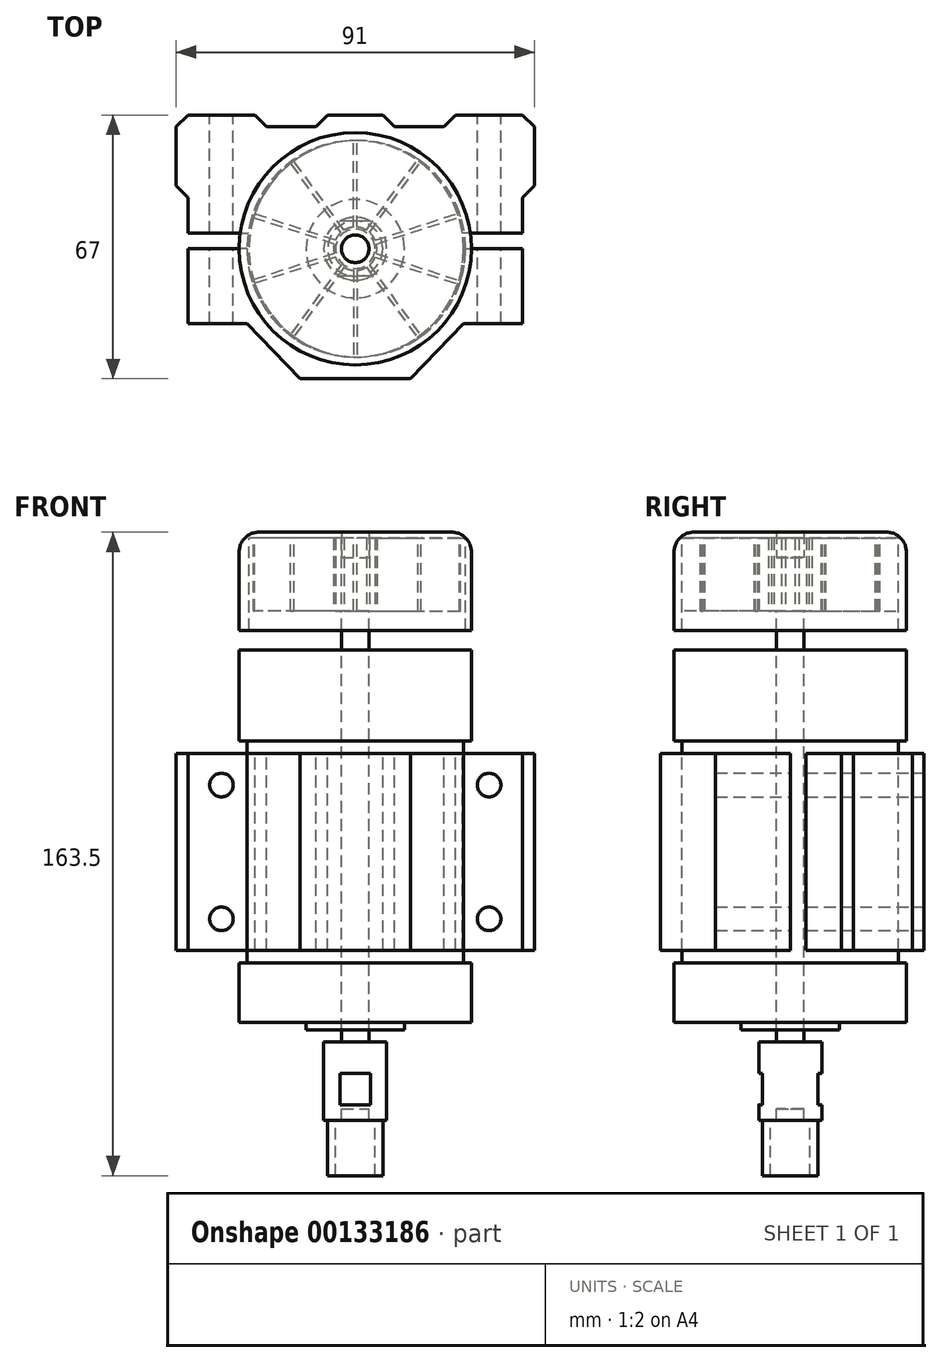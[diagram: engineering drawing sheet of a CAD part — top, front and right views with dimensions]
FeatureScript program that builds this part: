
annotation { "Feature Type Name" : "Feature", "Feature Type Description" : "" }
export const myFeature = defineFeature(function(context is Context, id is Id, definition is map)
    precondition{}
    {
        {
            var Q0;
            Q0=qCreatedBy(makeId("Top.planeOp"),FACE);
            var sketch = newSketch(context, id + "F0", { "sketchPlane" : qUnion([Q0])});
            skCircle(sketch, "E0", {"center": v(0, 0) * mm, "radius": 27.5 * mm});
            skLineSegment(sketch, "E1", {"start": v(-27.5, 0) * mm, "end": v(-42.5, 0) * mm});
            skLineSegment(sketch, "E2", {"start": v(-42.5, 0) * mm, "end": v(-42.5, -19) * mm});
            skLineSegment(sketch, "E3", {"start": v(-42.5, -19) * mm, "end": v(-27.5, -19) * mm});
            skLineSegment(sketch, "E4", {"start": v(-27.5, -19) * mm, "end": v(-14, -33) * mm});
            skLineSegment(sketch, "E5", {"start": v(-14, -33) * mm, "end": v(0, -33) * mm});
            skLineSegment(sketch, "E6.MirrorCS", {"start": v(14, -33) * mm, "end": v(0, -33) * mm});
            skLineSegment(sketch, "E7.MirrorCS", {"start": v(27.5, -19) * mm, "end": v(14, -33) * mm});
            skLineSegment(sketch, "E8.MirrorCS", {"start": v(42.5, -19) * mm, "end": v(27.5, -19) * mm});
            skLineSegment(sketch, "E9.MirrorCS", {"start": v(27.5, 0) * mm, "end": v(42.5, 0) * mm});
            skLineSegment(sketch, "E10.MirrorCS", {"start": v(42.5, 0) * mm, "end": v(42.5, -19) * mm});
            skLineSegment(sketch, "E11", {"start": v(-42.5, 4) * mm, "end": v(-42.5, 13) * mm});
            skLineSegment(sketch, "E12", {"start": v(-42.5, 13) * mm, "end": v(-45.5, 16) * mm});
            skLineSegment(sketch, "E13", {"start": v(-45.5, 16) * mm, "end": v(-45.5, 31) * mm});
            skLineSegment(sketch, "E14", {"start": v(-45.5, 31) * mm, "end": v(-42.5, 34) * mm});
            skLineSegment(sketch, "E15", {"start": v(-42.5, 34) * mm, "end": v(-25.5, 34) * mm});
            skLineSegment(sketch, "E16", {"start": v(-25.5, 34) * mm, "end": v(-22.5, 31) * mm});
            skLineSegment(sketch, "E17", {"start": v(-22.5, 31) * mm, "end": v(-10, 31) * mm});
            skLineSegment(sketch, "E18", {"start": v(-10, 31) * mm, "end": v(-7, 34) * mm});
            skLineSegment(sketch, "E19", {"start": v(-7, 34) * mm, "end": v(0, 34) * mm});
            skLineSegment(sketch, "E20", {"start": v(-42.5, 4) * mm, "end": v(-27.2, 4) * mm});
            skLineSegment(sketch, "E21.MirrorCS", {"start": v(25.5, 34) * mm, "end": v(22.5, 31) * mm});
            skLineSegment(sketch, "E22.MirrorCS", {"start": v(42.5, 34) * mm, "end": v(25.5, 34) * mm});
            skLineSegment(sketch, "E23.MirrorCS", {"start": v(45.5, 31) * mm, "end": v(42.5, 34) * mm});
            skLineSegment(sketch, "E24.MirrorCS", {"start": v(45.5, 16) * mm, "end": v(45.5, 31) * mm});
            skLineSegment(sketch, "E25.MirrorCS", {"start": v(7, 34) * mm, "end": v(0, 34) * mm});
            skLineSegment(sketch, "E26.MirrorCS", {"start": v(10, 31) * mm, "end": v(7, 34) * mm});
            skLineSegment(sketch, "E27.MirrorCS", {"start": v(22.5, 31) * mm, "end": v(10, 31) * mm});
            skLineSegment(sketch, "E28.MirrorCS", {"start": v(42.5, 13) * mm, "end": v(45.5, 16) * mm});
            skLineSegment(sketch, "E29.MirrorCS", {"start": v(42.5, 4) * mm, "end": v(42.5, 13) * mm});
            skLineSegment(sketch, "E30.MirrorCS", {"start": v(42.5, 4) * mm, "end": v(27.2, 4) * mm});
            skSolve(sketch);
        }
        {
            var Q0;
            Q0=makeQuery(id+"F0.imprint","IMPRINT",FACE,{"disambiguationData":[TD([[makeQuery(id+"F0.imprint","IMPRINT",EDGE,{"derivedFrom":sQuery(id+"F0.wireOp",EDGE,"E0")}),1.0]])]});
            extrude(context, id + "F1", {"entities" : qUnion([Q0]), "oppositeDirection" : true, "depth" : 56.5 * mm, "symmetric" : true});
        }
        {
            var Q0;
            Q0=makeQuery(id+"F1.opExtrude","CAP_FACE",FACE,{"disambiguationData":[OSD([sQuery(id+"F0.wireOp",EDGE,"E0")])],"isStart":true});
            var sketch = newSketch(context, id + "F2", { "sketchPlane" : qUnion([Q0])});
            skCircle(sketch, "E31.0", {"center": v(0, 0) * mm, "radius": 29.5 * mm});
            skSolve(sketch);
        }
        {
            var Q0;
            Q0=makeQuery(id+"F2.imprint","IMPRINT",FACE,{"disambiguationData":[TD([[makeQuery(id+"F2.imprint","IMPRINT",EDGE,{"derivedFrom":sQuery(id+"F2.wireOp",EDGE,"E31.0")}),1.0]])]});
            var Q1;
            Q1=makeQuery(id+"F2.imprint","IMPRINT",FACE,{"disambiguationData":[TD([[makeQuery(id+"F2.imprint","IMPRINT",EDGE,{"derivedFrom":makeQuery(id+"F1.opExtrude","CAP_EDGE",EDGE,{"disambiguationData":[OSD([sQuery(id+"F0.wireOp",EDGE,"E0")])],"isStart":true})}),1.0]])]});
            extrude(context, id + "F3", {"entities" : qUnion([Q0, Q1]), "operationType" : NewBodyOperationType.ADD, "depth" : 23 * mm});
        }
        {
            var Q0;
            Q0=makeQuery(id+"F1.opExtrude","CAP_FACE",FACE,{"disambiguationData":[OSD([sQuery(id+"F0.wireOp",EDGE,"E0")])],"isStart":false});
            var sketch = newSketch(context, id + "F4", { "sketchPlane" : qUnion([Q0])});
            skCircle(sketch, "E32.0", {"center": v(0, 0) * mm, "radius": 29.5 * mm});
            skSolve(sketch);
        }
        {
            var Q0;
            Q0=makeQuery(id+"F4.imprint","IMPRINT",FACE,{"disambiguationData":[TD([[makeQuery(id+"F4.imprint","IMPRINT",EDGE,{"derivedFrom":sQuery(id+"F4.wireOp",EDGE,"E32.0")}),1.0]])]});
            var Q1;
            Q1=makeQuery(id+"F4.imprint","IMPRINT",FACE,{"disambiguationData":[TD([[makeQuery(id+"F4.imprint","IMPRINT",EDGE,{"derivedFrom":makeQuery(id+"F1.opExtrude","CAP_EDGE",EDGE,{"disambiguationData":[OSD([sQuery(id+"F0.wireOp",EDGE,"E0")])],"isStart":false})}),-1.0]])]});
            extrude(context, id + "F5", {"entities" : qUnion([Q0, Q1]), "operationType" : NewBodyOperationType.ADD, "depth" : 15 * mm});
        }
        {
            var Q0;
            Q0=makeQuery(id+"F5.opExtrude","CAP_FACE",FACE,{"disambiguationData":[OSD([sQuery(id+"F4.wireOp",EDGE,"E32.0")])],"isStart":false});
            var sketch = newSketch(context, id + "F6", { "sketchPlane" : qUnion([Q0])});
            skCircle(sketch, "E33", {"center": v(0, 0) * mm, "radius": 12.5 * mm});
            skSolve(sketch);
        }
        {
            var Q0;
            Q0=makeQuery(id+"F6.imprint","IMPRINT",FACE,{"disambiguationData":[TD([[makeQuery(id+"F6.imprint","IMPRINT",EDGE,{"derivedFrom":sQuery(id+"F6.wireOp",EDGE,"E33")}),1.0]])]});
            extrude(context, id + "F7", {"entities" : qUnion([Q0]), "operationType" : NewBodyOperationType.ADD, "depth" : 2 * mm});
        }
        {
            var Q0;
            Q0=makeQuery(id+"F7.opExtrude","CAP_FACE",FACE,{"disambiguationData":[OSD([sQuery(id+"F6.wireOp",EDGE,"E33")])],"isStart":false});
            var sketch = newSketch(context, id + "F8", { "sketchPlane" : qUnion([Q0])});
            skCircle(sketch, "E34", {"center": v(0, 0) * mm, "radius": 3.5 * mm});
            skSolve(sketch);
        }
        {
            var Q0;
            Q0=makeQuery(id+"F8.imprint","IMPRINT",FACE,{"disambiguationData":[TD([[makeQuery(id+"F8.imprint","IMPRINT",EDGE,{"derivedFrom":sQuery(id+"F8.wireOp",EDGE,"E34")}),1.0]])]});
            extrude(context, id + "F9", {"entities" : qUnion([Q0]), "depth" : 20 * mm, "hasSecondDirection" : true, "secondDirectionOppositeDirection" : true, "secondDirectionDepth" : 120 * mm});
        }
        {
            var Q0;
            Q0=makeQuery(id+"F7.opExtrude","CAP_FACE",FACE,{"disambiguationData":[OSD([sQuery(id+"F6.wireOp",EDGE,"E33")])],"isStart":false});
            cPlane(context, id + "F10", {"entities" : qUnion([Q0]), "cplaneType" : CPlaneType.OFFSET, "offset" : 3 * mm, "width" : 150 * mm, "height" : 150 * mm});
        }
        {
            var Q0;
            Q0=qCreatedBy(id+"F10.planeOp",FACE);
            var sketch = newSketch(context, id + "F11", { "sketchPlane" : qUnion([Q0])});
            skCircle(sketch, "E35", {"center": v(0, 0) * mm, "radius": 8 * mm});
            skCircle(sketch, "E36", {"center": v(0, 0) * mm, "radius": 3.5 * mm});
            skSolve(sketch);
        }
        {
            var Q0;
            Q0=makeQuery(id+"F11.imprint","IMPRINT",FACE,{"disambiguationData":[TD([[makeQuery(id+"F11.imprint","IMPRINT",EDGE,{"derivedFrom":sQuery(id+"F11.wireOp",EDGE,"E35")}),1.0]])]});
            extrude(context, id + "F12", {"entities" : qUnion([Q0]), "operationType" : NewBodyOperationType.ADD, "depth" : 20 * mm});
        }
        {
            var Q0;
            Q0=qCreatedBy(makeId("Right.planeOp"),FACE);
            var sketch = newSketch(context, id + "F13", { "sketchPlane" : qUnion([Q0])});
            skLineSegment(sketch, "E37.bottom", {"start": v(12.32, -56.25) * mm, "end": v(7, -56.25) * mm});
            skLineSegment(sketch, "E37.top", {"start": v(12.32, -64.25) * mm, "end": v(7, -64.25) * mm});
            skLineSegment(sketch, "E37.left", {"start": v(12.32, -56.25) * mm, "end": v(12.32, -64.25) * mm});
            skLineSegment(sketch, "E37.right", {"start": v(7, -56.25) * mm, "end": v(7, -64.25) * mm});
            skLineSegment(sketch, "E38", {"start": v(0, -59.62) * mm, "end": v(0, -108.48) * mm, "construction": true});
            skLineSegment(sketch, "E39.MirrorCS", {"start": v(-12.32, -56.25) * mm, "end": v(-7, -56.25) * mm});
            skLineSegment(sketch, "E40.MirrorCS", {"start": v(-12.32, -64.25) * mm, "end": v(-7, -64.25) * mm});
            skLineSegment(sketch, "E41.MirrorCS", {"start": v(-12.32, -56.25) * mm, "end": v(-12.32, -64.25) * mm});
            skLineSegment(sketch, "E42.MirrorCS", {"start": v(-7, -56.25) * mm, "end": v(-7, -64.25) * mm});
            skSolve(sketch);
        }
        {
            var Q0;
            Q0=makeQuery(id+"F13.imprint","IMPRINT",FACE,{"disambiguationData":[TD([[makeQuery(id+"F13.imprint","IMPRINT",EDGE,{"derivedFrom":sQuery(id+"F13.wireOp",EDGE,"E37.bottom")}),1.0]])]});
            var Q1;
            Q1=makeQuery(id+"F13.imprint","IMPRINT",FACE,{"disambiguationData":[TD([[makeQuery(id+"F13.imprint","IMPRINT",EDGE,{"derivedFrom":sQuery(id+"F13.wireOp",EDGE,"E39.MirrorCS")}),-1.0]])]});
            extrude(context, id + "F14", {"entities" : qUnion([Q0, Q1]), "operationType" : NewBodyOperationType.REMOVE, "depth" : 10 * mm, "symmetric" : true});
        }
        {
            var Q0;
            Q0=makeQuery(id+"F12.opExtrude","CAP_FACE",FACE,{"disambiguationData":[OSD([sQuery(id+"F11.wireOp",EDGE,"E35"),sQuery(id+"F11.wireOp",EDGE,"E36")])],"isStart":false});
            var sketch = newSketch(context, id + "F15", { "sketchPlane" : qUnion([Q0])});
            skCircle(sketch, "E43", {"center": v(0, 0) * mm, "radius": 7 * mm});
            skCircle(sketch, "E44.0", {"center": v(0, 0) * mm, "radius": 5 * mm});
            skSolve(sketch);
        }
        {
            var Q0;
            Q0=makeQuery(id+"F15.imprint","IMPRINT",FACE,{"disambiguationData":[TD([[makeQuery(id+"F15.imprint","IMPRINT",EDGE,{"derivedFrom":sQuery(id+"F15.wireOp",EDGE,"E43")}),1.0]])]});
            extrude(context, id + "F16", {"entities" : qUnion([Q0]), "operationType" : NewBodyOperationType.ADD, "depth" : 14 * mm});
        }
        {
            var Q0;
            Q0=makeQuery(id+"F3.opExtrude","CAP_FACE",FACE,{"disambiguationData":[OSD([sQuery(id+"F2.wireOp",EDGE,"E31.0")])],"isStart":false});
            cPlane(context, id + "F17", {"entities" : qUnion([Q0]), "cplaneType" : CPlaneType.OFFSET, "offset" : 10 * mm, "width" : 150 * mm, "height" : 150 * mm});
        }
        {
            var Q0;
            Q0=qCreatedBy(id+"F17.planeOp",FACE);
            var sketch = newSketch(context, id + "F18", { "sketchPlane" : qUnion([Q0])});
            skLineSegment(sketch, "E45.bottom", {"start": v(-0.5, -3.78) * mm, "end": v(0.5, -3.78) * mm});
            skLineSegment(sketch, "E45.top", {"start": v(-0.5, -29.13) * mm, "end": v(0.5, -29.13) * mm});
            skLineSegment(sketch, "E45.left", {"start": v(-0.5, -5.48) * mm, "end": v(-0.5, -29.13) * mm});
            skLineSegment(sketch, "E45.right", {"start": v(0.5, -5.48) * mm, "end": v(0.5, -29.13) * mm});
            skLineSegment(sketch, "E46.1.0", {"start": v(3.62, -4.14) * mm, "end": v(17.53, -23.27) * mm});
            skLineSegment(sketch, "E46.1.1", {"start": v(2.81, -4.73) * mm, "end": v(16.72, -23.86) * mm});
            skLineSegment(sketch, "E46.1.2", {"start": v(16.72, -23.86) * mm, "end": v(17.53, -23.27) * mm});
            skLineSegment(sketch, "E46.1.3", {"start": v(1.82, -3.35) * mm, "end": v(2.63, -2.76) * mm});
            skLineSegment(sketch, "E46.2.0", {"start": v(5.36, -1.22) * mm, "end": v(27.86, -8.53) * mm});
            skLineSegment(sketch, "E46.2.1", {"start": v(5.05, -2.17) * mm, "end": v(27.55, -9.48) * mm});
            skLineSegment(sketch, "E46.2.2", {"start": v(27.55, -9.48) * mm, "end": v(27.86, -8.53) * mm});
            skLineSegment(sketch, "E46.2.3", {"start": v(3.44, -1.64) * mm, "end": v(3.75, -0.7) * mm});
            skLineSegment(sketch, "E46.3.0", {"start": v(5.05, 2.17) * mm, "end": v(27.55, 9.48) * mm});
            skLineSegment(sketch, "E46.3.1", {"start": v(5.36, 1.22) * mm, "end": v(27.86, 8.53) * mm});
            skLineSegment(sketch, "E46.3.2", {"start": v(27.86, 8.53) * mm, "end": v(27.55, 9.48) * mm});
            skLineSegment(sketch, "E46.3.3", {"start": v(3.75, 0.7) * mm, "end": v(3.44, 1.64) * mm});
            skLineSegment(sketch, "E46.4.0", {"start": v(2.81, 4.73) * mm, "end": v(16.72, 23.86) * mm});
            skLineSegment(sketch, "E46.4.1", {"start": v(3.62, 4.14) * mm, "end": v(17.53, 23.27) * mm});
            skLineSegment(sketch, "E46.4.2", {"start": v(17.53, 23.27) * mm, "end": v(16.72, 23.86) * mm});
            skLineSegment(sketch, "E46.4.3", {"start": v(2.63, 2.76) * mm, "end": v(1.82, 3.35) * mm});
            skLineSegment(sketch, "E46.5.0", {"start": v(-0.5, 5.48) * mm, "end": v(-0.5, 29.13) * mm});
            skLineSegment(sketch, "E46.5.1", {"start": v(0.5, 5.48) * mm, "end": v(0.5, 29.13) * mm});
            skLineSegment(sketch, "E46.5.2", {"start": v(0.5, 29.13) * mm, "end": v(-0.5, 29.13) * mm});
            skLineSegment(sketch, "E46.5.3", {"start": v(0.5, 3.78) * mm, "end": v(-0.5, 3.78) * mm});
            skLineSegment(sketch, "E46.6.0", {"start": v(-3.62, 4.14) * mm, "end": v(-17.53, 23.27) * mm});
            skLineSegment(sketch, "E46.6.1", {"start": v(-2.81, 4.73) * mm, "end": v(-16.72, 23.86) * mm});
            skLineSegment(sketch, "E46.6.2", {"start": v(-16.72, 23.86) * mm, "end": v(-17.53, 23.27) * mm});
            skLineSegment(sketch, "E46.6.3", {"start": v(-1.82, 3.35) * mm, "end": v(-2.63, 2.76) * mm});
            skLineSegment(sketch, "E46.7.0", {"start": v(-5.36, 1.22) * mm, "end": v(-27.86, 8.53) * mm});
            skLineSegment(sketch, "E46.7.1", {"start": v(-5.05, 2.17) * mm, "end": v(-27.55, 9.48) * mm});
            skLineSegment(sketch, "E46.7.2", {"start": v(-27.55, 9.48) * mm, "end": v(-27.86, 8.53) * mm});
            skLineSegment(sketch, "E46.7.3", {"start": v(-3.44, 1.64) * mm, "end": v(-3.75, 0.7) * mm});
            skLineSegment(sketch, "E46.8.0", {"start": v(-5.05, -2.17) * mm, "end": v(-27.55, -9.48) * mm});
            skLineSegment(sketch, "E46.8.1", {"start": v(-5.36, -1.22) * mm, "end": v(-27.86, -8.53) * mm});
            skLineSegment(sketch, "E46.8.2", {"start": v(-27.86, -8.53) * mm, "end": v(-27.55, -9.48) * mm});
            skLineSegment(sketch, "E46.8.3", {"start": v(-3.75, -0.7) * mm, "end": v(-3.44, -1.64) * mm});
            skLineSegment(sketch, "E46.9.0", {"start": v(-2.81, -4.73) * mm, "end": v(-16.72, -23.86) * mm});
            skLineSegment(sketch, "E46.9.1", {"start": v(-3.62, -4.14) * mm, "end": v(-17.53, -23.27) * mm});
            skLineSegment(sketch, "E46.9.2", {"start": v(-17.53, -23.27) * mm, "end": v(-16.72, -23.86) * mm});
            skLineSegment(sketch, "E46.9.3", {"start": v(-2.63, -2.76) * mm, "end": v(-1.82, -3.35) * mm});
            skPoint(sketch, "E46.center", {"position": v(0, 0) * mm});
            skCircle(sketch, "E47", {"center": v(0, 0) * mm, "radius": 3.5 * mm});
            skArc(sketch, "E48", {"start": v(-5.36, 1.22) * mm, "mid": v(-5.5, 0) * mm, "end": v(-5.36, -1.22) * mm});
            skArc(sketch, "E49.trimOffspring", {"start": v(-3.62, 4.14) * mm, "mid": v(-4.45, 3.23) * mm, "end": v(-5.05, 2.17) * mm});
            skArc(sketch, "E50.trimOffspring", {"start": v(-0.5, 5.48) * mm, "mid": v(-1.7, 5.23) * mm, "end": v(-2.81, 4.73) * mm});
            skArc(sketch, "E51.trimOffspring", {"start": v(2.81, 4.73) * mm, "mid": v(1.7, 5.23) * mm, "end": v(0.5, 5.48) * mm});
            skArc(sketch, "E52.trimOffspring", {"start": v(5.05, 2.17) * mm, "mid": v(4.45, 3.23) * mm, "end": v(3.62, 4.14) * mm});
            skArc(sketch, "E53.trimOffspring", {"start": v(5.36, -1.22) * mm, "mid": v(5.5, 0) * mm, "end": v(5.36, 1.22) * mm});
            skArc(sketch, "E54.trimOffspring", {"start": v(3.62, -4.14) * mm, "mid": v(4.45, -3.23) * mm, "end": v(5.05, -2.17) * mm});
            skArc(sketch, "E55.trimOffspring", {"start": v(0.5, -5.48) * mm, "mid": v(1.7, -5.23) * mm, "end": v(2.81, -4.73) * mm});
            skArc(sketch, "E56.trimOffspring", {"start": v(-2.81, -4.73) * mm, "mid": v(-1.7, -5.23) * mm, "end": v(-0.5, -5.48) * mm});
            skArc(sketch, "E57.trimOffspring", {"start": v(-5.05, -2.17) * mm, "mid": v(-4.45, -3.23) * mm, "end": v(-3.62, -4.14) * mm});
            skSolve(sketch);
        }
        {
            var Q0;
            Q0=makeQuery(id+"F18.imprint","IMPRINT",FACE,{"disambiguationData":[TD([[makeQuery(id+"F18.imprint","IMPRINT",EDGE,{"derivedFrom":sQuery(id+"F18.wireOp",EDGE,"E45.top")}),1.0]])]});
            extrude(context, id + "F19", {"entities" : qUnion([Q0]), "operationType" : NewBodyOperationType.ADD, "depth" : 20 * mm});
        }
        {
            var Q0;
            Q0=makeQuery(id+"F19.opExtrude","CAP_FACE",FACE,{"disambiguationData":[OSD([sQuery(id+"F18.wireOp",EDGE,"E45.top"),sQuery(id+"F18.wireOp",EDGE,"E45.left"),sQuery(id+"F18.wireOp",EDGE,"E45.right"),sQuery(id+"F18.wireOp",EDGE,"E46.1.0"),sQuery(id+"F18.wireOp",EDGE,"E46.1.1"),sQuery(id+"F18.wireOp",EDGE,"E46.1.2"),sQuery(id+"F18.wireOp",EDGE,"E46.2.0"),sQuery(id+"F18.wireOp",EDGE,"E46.2.1"),sQuery(id+"F18.wireOp",EDGE,"E46.2.2"),sQuery(id+"F18.wireOp",EDGE,"E46.3.0"),sQuery(id+"F18.wireOp",EDGE,"E46.3.1"),sQuery(id+"F18.wireOp",EDGE,"E46.3.2"),sQuery(id+"F18.wireOp",EDGE,"E46.4.0"),sQuery(id+"F18.wireOp",EDGE,"E46.4.1"),sQuery(id+"F18.wireOp",EDGE,"E46.4.2"),sQuery(id+"F18.wireOp",EDGE,"E46.5.0"),sQuery(id+"F18.wireOp",EDGE,"E46.5.1"),sQuery(id+"F18.wireOp",EDGE,"E46.5.2"),sQuery(id+"F18.wireOp",EDGE,"E46.6.0"),sQuery(id+"F18.wireOp",EDGE,"E46.6.1"),sQuery(id+"F18.wireOp",EDGE,"E46.6.2"),sQuery(id+"F18.wireOp",EDGE,"E46.7.0"),sQuery(id+"F18.wireOp",EDGE,"E46.7.1"),sQuery(id+"F18.wireOp",EDGE,"E46.7.2"),sQuery(id+"F18.wireOp",EDGE,"E46.8.0"),sQuery(id+"F18.wireOp",EDGE,"E46.8.1"),sQuery(id+"F18.wireOp",EDGE,"E46.8.2"),sQuery(id+"F18.wireOp",EDGE,"E46.9.0"),sQuery(id+"F18.wireOp",EDGE,"E46.9.1"),sQuery(id+"F18.wireOp",EDGE,"E46.9.2"),sQuery(id+"F18.wireOp",EDGE,"E47"),sQuery(id+"F18.wireOp",EDGE,"E48"),sQuery(id+"F18.wireOp",EDGE,"E49.trimOffspring"),sQuery(id+"F18.wireOp",EDGE,"E50.trimOffspring"),sQuery(id+"F18.wireOp",EDGE,"E51.trimOffspring"),sQuery(id+"F18.wireOp",EDGE,"E52.trimOffspring"),sQuery(id+"F18.wireOp",EDGE,"E53.trimOffspring"),sQuery(id+"F18.wireOp",EDGE,"E54.trimOffspring"),sQuery(id+"F18.wireOp",EDGE,"E55.trimOffspring"),sQuery(id+"F18.wireOp",EDGE,"E56.trimOffspring"),sQuery(id+"F18.wireOp",EDGE,"E57.trimOffspring")])],"isStart":false});
            var sketch = newSketch(context, id + "F20", { "sketchPlane" : qUnion([Q0])});
            skCircle(sketch, "E58", {"center": v(0, 0) * mm, "radius": 29.5 * mm});
            skSolve(sketch);
        }
        {
            var Q0;
            Q0=makeQuery(id+"F20.imprint","IMPRINT",FACE,{"disambiguationData":[TD([[makeQuery(id+"F20.imprint","IMPRINT",EDGE,{"derivedFrom":sQuery(id+"F20.wireOp",EDGE,"E58")}),1.0]])]});
            extrude(context, id + "F21", {"entities" : qUnion([Q0]), "operationType" : NewBodyOperationType.ADD, "oppositeDirection" : true, "depth" : 1.5 * mm});
        }
        {
            var Q0;
            {var subQ0=sQuery(id+"F18.wireOp",EDGE,"E57.trimOffspring");var subQ1=sQuery(id+"F18.wireOp",EDGE,"E56.trimOffspring");var subQ2=sQuery(id+"F18.wireOp",EDGE,"E55.trimOffspring");var subQ3=sQuery(id+"F18.wireOp",EDGE,"E54.trimOffspring");var subQ4=sQuery(id+"F18.wireOp",EDGE,"E53.trimOffspring");var subQ5=sQuery(id+"F18.wireOp",EDGE,"E52.trimOffspring");var subQ6=sQuery(id+"F18.wireOp",EDGE,"E51.trimOffspring");var subQ7=sQuery(id+"F18.wireOp",EDGE,"E50.trimOffspring");var subQ8=sQuery(id+"F18.wireOp",EDGE,"E49.trimOffspring");var subQ9=sQuery(id+"F18.wireOp",EDGE,"E48");var subQ10=sQuery(id+"F18.wireOp",EDGE,"E46.9.2");var subQ11=sQuery(id+"F18.wireOp",EDGE,"E46.9.1");var subQ12=sQuery(id+"F18.wireOp",EDGE,"E46.9.0");var subQ13=sQuery(id+"F18.wireOp",EDGE,"E46.8.2");var subQ14=sQuery(id+"F18.wireOp",EDGE,"E46.8.1");var subQ15=sQuery(id+"F18.wireOp",EDGE,"E46.8.0");var subQ16=sQuery(id+"F18.wireOp",EDGE,"E46.7.2");var subQ17=sQuery(id+"F18.wireOp",EDGE,"E46.7.1");var subQ18=sQuery(id+"F18.wireOp",EDGE,"E46.7.0");var subQ19=sQuery(id+"F18.wireOp",EDGE,"E46.6.2");var subQ20=sQuery(id+"F18.wireOp",EDGE,"E46.6.1");var subQ21=sQuery(id+"F18.wireOp",EDGE,"E46.6.0");var subQ22=sQuery(id+"F18.wireOp",EDGE,"E46.5.2");var subQ23=sQuery(id+"F18.wireOp",EDGE,"E46.5.1");var subQ24=sQuery(id+"F18.wireOp",EDGE,"E46.5.0");var subQ25=sQuery(id+"F18.wireOp",EDGE,"E46.4.2");var subQ26=sQuery(id+"F18.wireOp",EDGE,"E46.4.1");var subQ27=sQuery(id+"F18.wireOp",EDGE,"E46.4.0");var subQ28=sQuery(id+"F18.wireOp",EDGE,"E46.3.2");var subQ29=sQuery(id+"F18.wireOp",EDGE,"E46.3.1");var subQ30=sQuery(id+"F18.wireOp",EDGE,"E46.3.0");var subQ31=sQuery(id+"F18.wireOp",EDGE,"E46.2.2");var subQ32=sQuery(id+"F18.wireOp",EDGE,"E46.2.1");var subQ33=sQuery(id+"F18.wireOp",EDGE,"E46.2.0");var subQ34=sQuery(id+"F18.wireOp",EDGE,"E46.1.2");var subQ35=sQuery(id+"F18.wireOp",EDGE,"E46.1.1");var subQ36=sQuery(id+"F18.wireOp",EDGE,"E46.1.0");var subQ37=sQuery(id+"F18.wireOp",EDGE,"E45.right");var subQ38=sQuery(id+"F18.wireOp",EDGE,"E45.left");var subQ39=sQuery(id+"F18.wireOp",EDGE,"E45.top");Q0=makeQuery(id+"F21.boolean.opBoolean","MERGE",FACE,{"derivedFrom":[makeQuery(id+"F19.opExtrude","CAP_FACE",FACE,{"disambiguationData":[OSD([subQ39,subQ38,subQ37,subQ36,subQ35,subQ34,subQ33,subQ32,subQ31,subQ30,subQ29,subQ28,subQ27,subQ26,subQ25,subQ24,subQ23,subQ22,subQ21,subQ20,subQ19,subQ18,subQ17,subQ16,subQ15,subQ14,subQ13,subQ12,subQ11,subQ10,sQuery(id+"F18.wireOp",EDGE,"E47"),subQ9,subQ8,subQ7,subQ6,subQ5,subQ4,subQ3,subQ2,subQ1,subQ0])],"isStart":false}),makeQuery(id+"F21.opExtrude","CAP_FACE",FACE,{"disambiguationData":[OSD([subQ39,subQ38,subQ37,subQ36,subQ35,subQ34,subQ33,subQ32,subQ31,subQ30,subQ29,subQ28,subQ27,subQ26,subQ25,subQ24,subQ23,subQ22,subQ21,subQ20,subQ19,subQ18,subQ17,subQ16,subQ15,subQ14,subQ13,subQ12,subQ11,subQ10,subQ9,subQ8,subQ7,subQ6,subQ5,subQ4,subQ3,subQ2,subQ1,subQ0,sQuery(id+"F20.wireOp",EDGE,"E58")])],"isStart":true})]});}
            var sketch = newSketch(context, id + "F22", { "sketchPlane" : qUnion([Q0])});
            skCircle(sketch, "E59", {"center": v(0.5, 0) * mm, "radius": 27.5 * mm});
            skSolve(sketch);
        }
        {
            var Q0;
            Q0=makeQuery(id+"F22.imprint","IMPRINT",FACE,{"disambiguationData":[TD([[makeQuery(id+"F22.imprint","IMPRINT",EDGE,{"derivedFrom":sQuery(id+"F22.wireOp",EDGE,"E59")}),-1.0]])]});
            extrude(context, id + "F23", {"entities" : qUnion([Q0]), "operationType" : NewBodyOperationType.ADD, "oppositeDirection" : true, "depth" : 25 * mm});
        }
        {
            var Q0;
            Q0=makeQuery(id+"F21.opExtrude","CAP_EDGE",EDGE,{"disambiguationData":[OSD([sQuery(id+"F20.wireOp",EDGE,"E58")])],"isStart":true});
            fillet(context, id + "F24", {"entities" : qUnion([Q0]), "radius" : 5 * mm, "tangentPropagation" : true, "allowEdgeOverflow" : false});
        }
        {
            var Q0;
            {var subQ0=sQuery(id+"F0.wireOp",EDGE,"E1");Q0=makeQuery(id+"F0.imprint","IMPRINT",FACE,{"disambiguationData":[TD([[makeQuery(id+"F0.imprint","IMPRINT",EDGE,{"derivedFrom":subQ0}),1.0]])]});}
            var Q1;
            Q1=makeQuery(id+"F0.imprint","IMPRINT",FACE,{"disambiguationData":[TD([[makeQuery(id+"F0.imprint","IMPRINT",EDGE,{"derivedFrom":sQuery(id+"F0.wireOp",EDGE,"E11")}),-1.0]])]});
            extrude(context, id + "F25", {"entities" : qUnion([Q0, Q1]), "oppositeDirection" : true, "depth" : 50 * mm, "symmetric" : true});
        }
        {
            var Q0;
            Q0=makeQuery(id+"F25.opExtrude","SWEPT_FACE",FACE,{"disambiguationData":[OSD([sQuery(id+"F0.wireOp",EDGE,"E8.MirrorCS")])]});
            var sketch = newSketch(context, id + "F26", { "sketchPlane" : qUnion([Q0])});
            skPoint(sketch, "E60", {"position": v(34, 17) * mm});
            skPoint(sketch, "E61", {"position": v(34, -17) * mm});
            skPoint(sketch, "E62", {"position": v(-34, 17) * mm});
            skPoint(sketch, "E63", {"position": v(-34, -17) * mm});
            skSolve(sketch);
        }
        {
            var Q0;
            Q0=sQuery(id+"F26.wireOp",VERTEX,"E62");
            var Q1;
            Q1=sQuery(id+"F26.wireOp",VERTEX,"E63");
            var Q2;
            Q2=sQuery(id+"F26.wireOp",VERTEX,"E60");
            var Q3;
            Q3=sQuery(id+"F26.wireOp",VERTEX,"E61");
            var Q4;
            Q4=makeQuery(id+"F25.opExtrude","SWEPT_BODY",BODY,{"disambiguationData":[OSD([sQuery(id+"F0.wireOp",EDGE,"E0"),sQuery(id+"F0.wireOp",EDGE,"E1"),sQuery(id+"F0.wireOp",EDGE,"E2"),sQuery(id+"F0.wireOp",EDGE,"E3"),sQuery(id+"F0.wireOp",EDGE,"E4"),sQuery(id+"F0.wireOp",EDGE,"E5"),sQuery(id+"F0.wireOp",EDGE,"E6.MirrorCS"),sQuery(id+"F0.wireOp",EDGE,"E7.MirrorCS"),sQuery(id+"F0.wireOp",EDGE,"E8.MirrorCS"),sQuery(id+"F0.wireOp",EDGE,"E9.MirrorCS"),sQuery(id+"F0.wireOp",EDGE,"E10.MirrorCS")])]});
            var Q5;
            Q5=makeQuery(id+"F25.opExtrude","SWEPT_BODY",BODY,{"disambiguationData":[OSD([sQuery(id+"F0.wireOp",EDGE,"E0"),sQuery(id+"F0.wireOp",EDGE,"E11"),sQuery(id+"F0.wireOp",EDGE,"E12"),sQuery(id+"F0.wireOp",EDGE,"E13"),sQuery(id+"F0.wireOp",EDGE,"E14"),sQuery(id+"F0.wireOp",EDGE,"E15"),sQuery(id+"F0.wireOp",EDGE,"E16"),sQuery(id+"F0.wireOp",EDGE,"E17"),sQuery(id+"F0.wireOp",EDGE,"E18"),sQuery(id+"F0.wireOp",EDGE,"E19"),sQuery(id+"F0.wireOp",EDGE,"E20"),sQuery(id+"F0.wireOp",EDGE,"E21.MirrorCS"),sQuery(id+"F0.wireOp",EDGE,"E22.MirrorCS"),sQuery(id+"F0.wireOp",EDGE,"E23.MirrorCS"),sQuery(id+"F0.wireOp",EDGE,"E24.MirrorCS"),sQuery(id+"F0.wireOp",EDGE,"E25.MirrorCS"),sQuery(id+"F0.wireOp",EDGE,"E26.MirrorCS"),sQuery(id+"F0.wireOp",EDGE,"E27.MirrorCS"),sQuery(id+"F0.wireOp",EDGE,"E28.MirrorCS"),sQuery(id+"F0.wireOp",EDGE,"E29.MirrorCS"),sQuery(id+"F0.wireOp",EDGE,"E30.MirrorCS")])]});
            hole(context, id + "F27", {"style" : HoleStyle.SIMPLE, "endStyle" : HoleEndStyle.THROUGH, "holeDiameter" : 6 * mm, "locations" : qUnion([Q0, Q1, Q2, Q3]), "scope" : qUnion([Q4, Q5]), "isTappedThrough" : true, "startStyle" : HoleStartStyle.PART});
        }
    });
